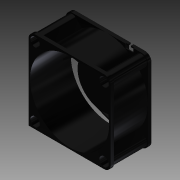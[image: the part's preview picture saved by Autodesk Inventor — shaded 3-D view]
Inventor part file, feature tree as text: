
AUTODESK INVENTOR PART (.ipt)
format: ipt  version: 2013 (Build 170138000, 138)  size: 279,552 bytes
history: native  units: mm (DEFAULTED — no unit token found)
features: sketch x10, extrude x9, plane x1, revolve x1, fillet x1, pattern_circular x1, other x1, projected_geometry x1
ambient origin geometry x8: Origin, YZ Plane, XZ Plane, XY Plane, X Axis, Y Axis, Z Axis, Center Point
bodies: Solid1 (feature_tree)
feature tree (25):
  extrude  "Extrusion1"  Depth=39.878mm
  plane  "Work Plane1"
  revolve  "Revolution1"  [1 undecoded]
  fillet  "Fillet1"  Radius=1.7018mm
  extrude  "Extrusion2"  TaperAngle=90.0deg  [1 undecoded]
  extrude  "Extrusion3"  Depth=4.572mm
  pattern_circular  "Circular Pattern1"  Count=4 Angle=360.0deg
  extrude  "Extrusion4"  Depth=38.481mm
  extrude  "fan support1"  Depth=0.635mm
  extrude  "fan support2"  Depth=3.81mm TaperAngle=0.0deg
  extrude  "fan support3"  Depth=8.001mm
  extrude  "fan support4"  Depth=4.0005mm
  extrude  "fan support5"  Depth=1.5875mm TaperAngle=0.0deg
  other  "fan interface"
  sketch  "Sketch1"  dims[d0=39.878mm d1=39.878mm]
  sketch  "Sketch2"  dims[d2=19.812mm d3=0.0mm d4=1.7018mm d5=1.7018mm]
  sketch  "Sketch3"  dims[d6=12.7mm d7=90.0deg]
  sketch  "Sketch4"  dims[d8=3.175mm d9=4.572mm]
  sketch  "Sketch5"  dims[d10=19.812mm d11=0.0mm]
  projected_geometry  "Projected Loop1"
  sketch  "Sketch6"  dims[d12=19.812mm d13=0.0mm d14=40.0mm d16=360.0deg]
  sketch  "Sketch7"  dims[d17=19.812mm d18=0.0mm d19=38.481mm]
  sketch  "Sketch8"  dims[d20=24.2824mm d21=0.635mm]
  sketch  "Sketch9"  dims[d23=0.635mm d24=3.81mm d25=0.0mm]
  sketch  "Sketch10"  dims[d26=5.08mm d27=8.001mm d28=4.0005mm d29=1.5875mm d30=0.0mm d31=22.896572mm d32=0.635mm d33=0.635mm d34=0.635mm d35=0.635mm d36=1.27mm d37=0.0mm d38=1.55575mm d39=0.0mm d40=1.55575mm d41=0.0mm d42=1.5875mm]
note: 2 required parameter values undecoded (feature->parameter linkage not recoverable at this tier; creation-order binding heuristic only, values carry confidence <= 0.55)